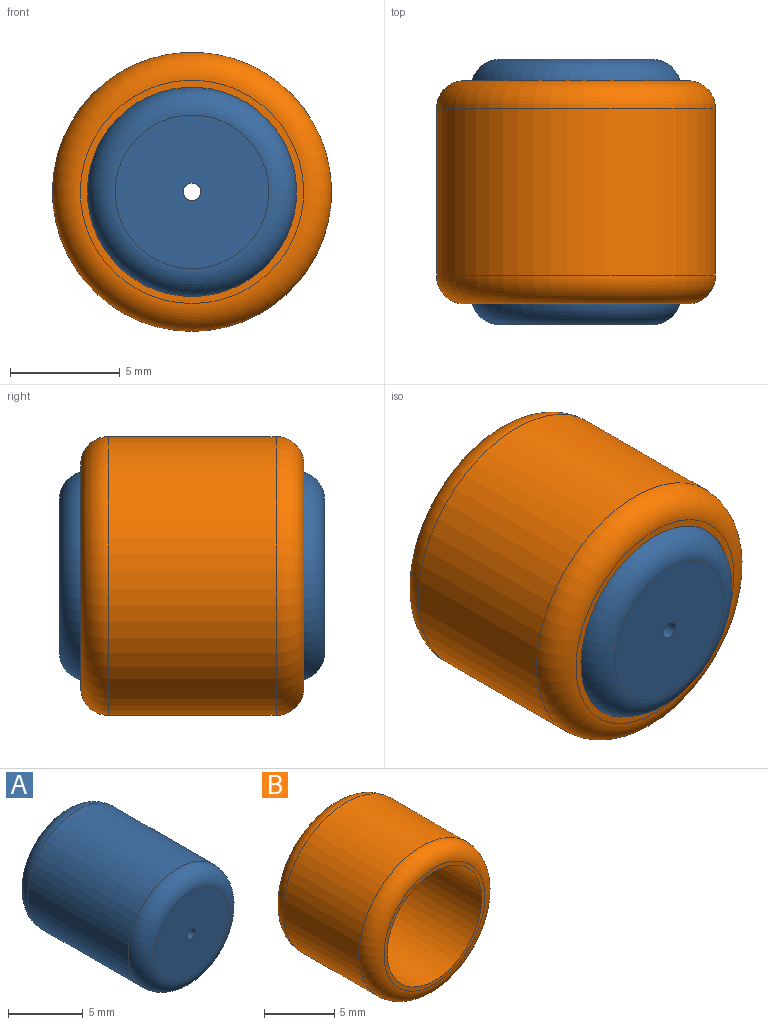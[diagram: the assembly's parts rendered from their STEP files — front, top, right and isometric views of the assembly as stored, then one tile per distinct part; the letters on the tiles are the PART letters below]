
ASSEMBLY  parts=2 mates=1
PART A: 6 faces, bbox 10.3x12.1x10.3 mm
  f0: cylinder r=4.76mm len=9.53mm, axis (0,1,0), area 285mm2, adj f3,f4
  f1: plane 6.99x6.99mm, normal (0,-1,0), area 37.8mm2, adj f4,f5
  f2: plane 6.99x6.99mm, normal (0,1,0), area 37.8mm2, adj f3,f5
  f3: torus R=3.49mm, axis (0,-1,0), area 53.9mm2, adj f0,f2
  f4: torus R=3.49mm, axis (0,-1,0), area 53.9mm2, adj f0,f1
  f5: cylinder r=0.4mm len=12.07mm, axis (0,1,0), area 30.1mm2, adj f1,f2
PART B: 6 faces, bbox 13.7x10.2x13.7 mm
  f0: cylinder r=4.76mm len=10.16mm, axis (0,1,0), area 304mm2, adj f2,f3
  f1: cylinder r=6.35mm len=12.7mm, axis (0,1,0), area 304mm2, adj f4,f5
  f2: plane 10.16x10.16mm, normal (0,-1,0), area 9.8mm2, adj f0,f5
  f3: plane 10.16x10.16mm, normal (0,1,0), area 9.8mm2, adj f0,f4
  f4: torus R=5.08mm, axis (0,-1,0), area 73.8mm2, adj f1,f3
  f5: torus R=5.08mm, axis (0,-1,0), area 73.8mm2, adj f1,f2
PLACE A t=(8.14,7.81,-4.41)mm
PLACE B t=(8.14,6.84,-4.41)mm
MATE fastened A.f0 <-> B.f1  axis (0,-1,0) through (8.14,-4.26,-4.41)mm
